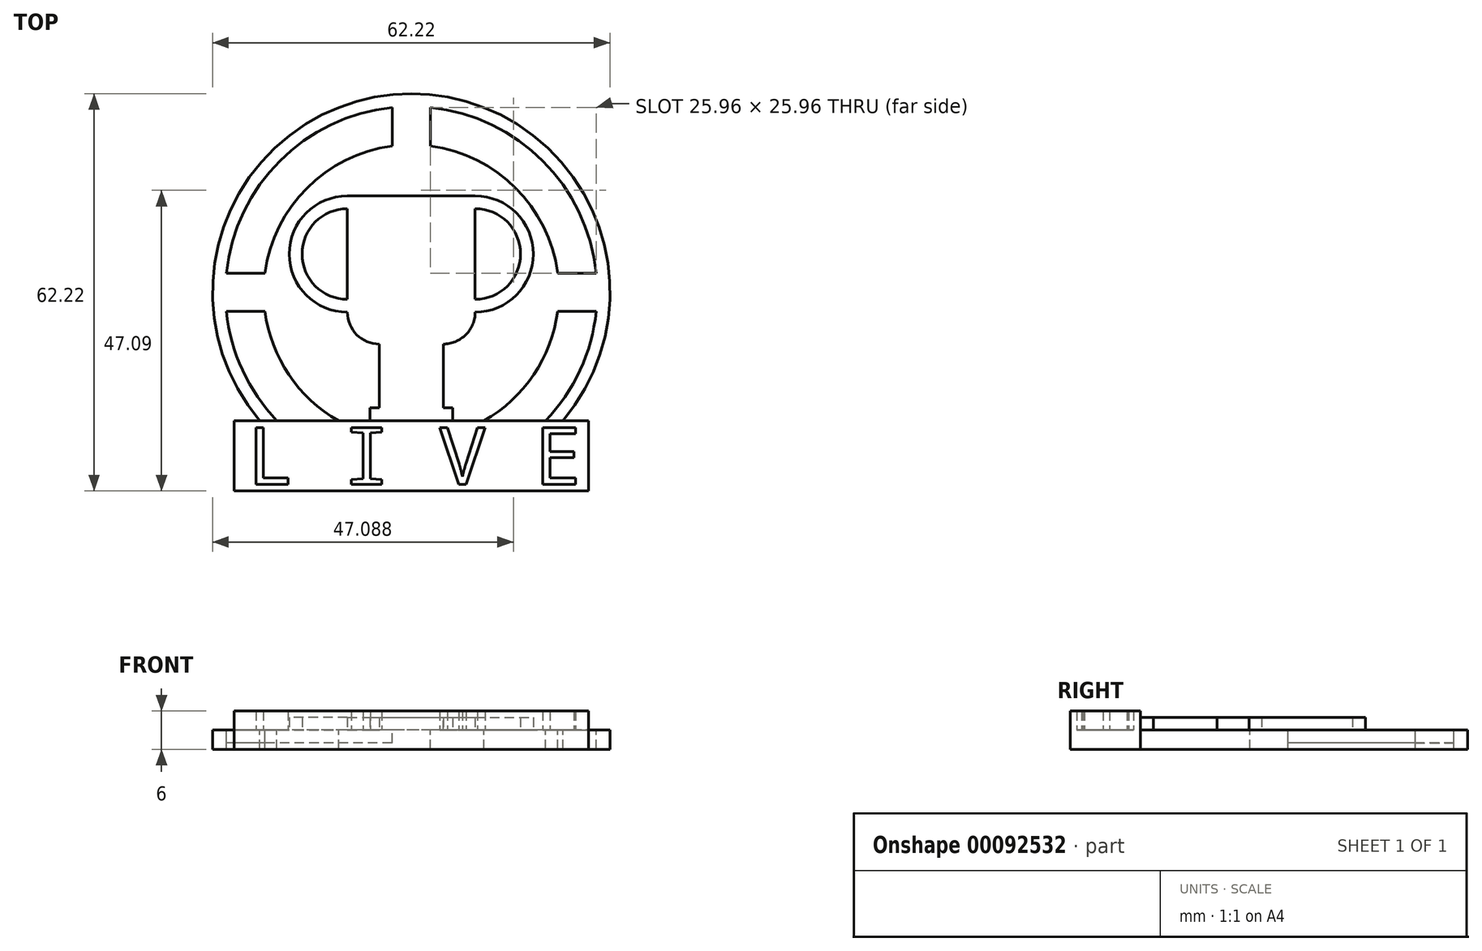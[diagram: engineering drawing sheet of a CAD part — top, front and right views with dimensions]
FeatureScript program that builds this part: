
annotation { "Feature Type Name" : "Feature", "Feature Type Description" : "" }
export const myFeature = defineFeature(function(context is Context, id is Id, definition is map)
    precondition{}
    {
        {
            var Q0;
            Q0=qCreatedBy(makeId("Top.planeOp"),FACE);
            var sketch = newSketch(context, id + "F0", { "sketchPlane" : qUnion([Q0])});
            skText(sketch, "E0", { "text": "L I V E", "fontName": "DroidSansMono.ttf"});
            skPoint(sketch, "E1", {"position": v(-23.74, 9) * mm});
            skPoint(sketch, "E2", {"position": v(23.74, 9) * mm});
            skPoint(sketch, "E3.third.point", {"position": v(14.12, 78.19) * mm});
            const initialGuessF0  = {"E0": [-0.02574, 0, 1, 0, 0.009]};
            skSetInitialGuess(sketch, initialGuessF0);
            skSolve(sketch);
        }
        {
            var Q0;
            Q0=qCreatedBy(makeId("Top.planeOp"),FACE);
            var sketch = newSketch(context, id + "F1", { "sketchPlane" : qUnion([Q0])});
            skLineSegment(sketch, "E4", {"start": v(-27.74, -1) * mm, "end": v(27.74, -1) * mm});
            skLineSegment(sketch, "E5", {"start": v(27.74, -1) * mm, "end": v(27.74, 10) * mm});
            skLineSegment(sketch, "E6", {"start": v(27.74, 10) * mm, "end": v(-27.74, 10) * mm});
            skLineSegment(sketch, "E7", {"start": v(-27.74, 10) * mm, "end": v(-27.74, -1) * mm});
            skSolve(sketch);
        }
        {
            var Q0;
            Q0 = qSketchRegion(id + "F1", true);
            extrude(context, id + "F2", {"entities" : qUnion([Q0]), "oppositeDirection" : true, "depth" : 3 * mm});
        }
        {
            var Q0;
            Q0=qCreatedBy(makeId("Top.planeOp"),FACE);
            var sketch = newSketch(context, id + "F3", { "sketchPlane" : qUnion([Q0])});
            skPoint(sketch, "E8", {"position": v(-23.74, 10) * mm});
            skPoint(sketch, "E9", {"position": v(23.74, 10) * mm});
            skArc(sketch, "E10", {"start": v(23.74, 10) * mm, "mid": v(0, 61.22) * mm, "end": v(-23.74, 10) * mm});
            skPoint(sketch, "E10.third.point", {"position": v(0, 61.22) * mm});
            skLineSegment(sketch, "E11", {"start": v(0, 30.11) * mm, "end": v(0, 61.22) * mm, "construction": true});
            skArc(sketch, "E12", {"start": v(21.05, 10) * mm, "mid": v(26.43, 17.9) * mm, "end": v(28.96, 27.11) * mm});
            skLineSegment(sketch, "E13", {"start": v(-31.11, 30.11) * mm, "end": v(0, 30.11) * mm, "construction": true});
            skArc(sketch, "E14", {"start": v(11.39, 10) * mm, "mid": v(19.17, 17.2) * mm, "end": v(22.92, 27.11) * mm});
            skLineSegment(sketch, "E15", {"start": v(-23.74, 10) * mm, "end": v(23.74, 10) * mm});
            skLineSegment(sketch, "E16.trimOffspring", {"start": v(-3, 53.03) * mm, "end": v(-3, 59.07) * mm});
            skLineSegment(sketch, "E17.trimOffspring", {"start": v(3, 53.03) * mm, "end": v(3, 59.07) * mm});
            skLineSegment(sketch, "E18.trimOffspring", {"start": v(-22.92, 33.11) * mm, "end": v(-28.96, 33.11) * mm});
            skLineSegment(sketch, "E19.trimOffspring", {"start": v(-22.92, 27.11) * mm, "end": v(-28.96, 27.11) * mm});
            skArc(sketch, "E20.trimOffspring", {"start": v(-22.92, 27.11) * mm, "mid": v(-19.17, 17.2) * mm, "end": v(-11.39, 10) * mm});
            skArc(sketch, "E21.trimOffspring", {"start": v(-28.96, 27.11) * mm, "mid": v(-26.43, 17.9) * mm, "end": v(-21.05, 10) * mm});
            skArc(sketch, "E22.trimOffspring", {"start": v(-3, 53.03) * mm, "mid": v(-16.34, 46.45) * mm, "end": v(-22.92, 33.11) * mm});
            skArc(sketch, "E23.trimOffspring", {"start": v(-3, 59.07) * mm, "mid": v(-20.59, 50.7) * mm, "end": v(-28.96, 33.11) * mm});
            skLineSegment(sketch, "E24.trimOffspring", {"start": v(22.92, 33.11) * mm, "end": v(28.96, 33.11) * mm});
            skLineSegment(sketch, "E25.trimOffspring", {"start": v(22.92, 27.11) * mm, "end": v(28.96, 27.11) * mm});
            skArc(sketch, "E26.trimOffspring", {"start": v(22.92, 33.11) * mm, "mid": v(16.34, 46.45) * mm, "end": v(3, 53.03) * mm});
            skArc(sketch, "E27.trimOffspring", {"start": v(28.96, 33.11) * mm, "mid": v(20.59, 50.7) * mm, "end": v(3, 59.07) * mm});
            skSolve(sketch);
        }
        {
            var Q0;
            {var subQ1=sQuery(id+"F3.wireOp",EDGE,"E10");Q0=makeQuery(id+"F3.imprint","IMPRINT",FACE,{"disambiguationData":[TD([[makeQuery(id+"F3.imprint","IMPRINT",EDGE,{"derivedFrom":subQ1}),1.0]])]});}
            var Q1;
            Q1=makeQuery(id+"F2.opExtrude","CAP_FACE",FACE,{"disambiguationData":[OSD([sQuery(id+"F1.wireOp",EDGE,"E4"),sQuery(id+"F1.wireOp",EDGE,"E5"),sQuery(id+"F1.wireOp",EDGE,"E6"),sQuery(id+"F1.wireOp",EDGE,"E7")])],"isStart":false});
            extrude(context, id + "F4", {"entities" : qUnion([Q0]), "operationType" : NewBodyOperationType.ADD, "oppositeDirection" : true, "endBoundEntityFace" : qUnion([Q1]), "depth" : 3 * mm});
        }
        {
            var Q0;
            Q0=makeQuery(id+"F4.boolean.opBoolean","MERGE",FACE,{"derivedFrom":[makeQuery(id+"F2.opExtrude","CAP_FACE",FACE,{"disambiguationData":[OSD([sQuery(id+"F1.wireOp",EDGE,"E4"),sQuery(id+"F1.wireOp",EDGE,"E5"),sQuery(id+"F1.wireOp",EDGE,"E6"),sQuery(id+"F1.wireOp",EDGE,"E7")])],"isStart":true}),makeQuery(id+"F4.opExtrude","CAP_FACE",FACE,{"disambiguationData":[OSD([sQuery(id+"F3.wireOp",EDGE,"E10"),sQuery(id+"F3.wireOp",EDGE,"E12"),sQuery(id+"F3.wireOp",EDGE,"E14"),sQuery(id+"F3.wireOp",EDGE,"E15"),sQuery(id+"F3.wireOp",EDGE,"E16.trimOffspring"),sQuery(id+"F3.wireOp",EDGE,"E17.trimOffspring"),sQuery(id+"F3.wireOp",EDGE,"E18.trimOffspring"),sQuery(id+"F3.wireOp",EDGE,"E19.trimOffspring"),sQuery(id+"F3.wireOp",EDGE,"E20.trimOffspring"),sQuery(id+"F3.wireOp",EDGE,"E21.trimOffspring"),sQuery(id+"F3.wireOp",EDGE,"E22.trimOffspring"),sQuery(id+"F3.wireOp",EDGE,"E23.trimOffspring"),sQuery(id+"F3.wireOp",EDGE,"E24.trimOffspring"),sQuery(id+"F3.wireOp",EDGE,"E25.trimOffspring"),sQuery(id+"F3.wireOp",EDGE,"E26.trimOffspring"),sQuery(id+"F3.wireOp",EDGE,"E27.trimOffspring")])],"isStart":true})]});
            var sketch = newSketch(context, id + "F5", { "sketchPlane" : qUnion([Q0])});
            skLineSegment(sketch, "E28.bottom", {"start": v(-6.5, 12) * mm, "end": v(-5, 12) * mm});
            skLineSegment(sketch, "E28.top", {"start": v(-6.5, 10) * mm, "end": v(6.5, 10) * mm});
            skLineSegment(sketch, "E28.left", {"start": v(-6.5, 12) * mm, "end": v(-6.5, 10) * mm});
            skLineSegment(sketch, "E28.right", {"start": v(6.5, 12) * mm, "end": v(6.5, 10) * mm});
            skLineSegment(sketch, "E29", {"start": v(11.39, 10) * mm, "end": v(11.39, 15) * mm, "construction": true});
            skLineSegment(sketch, "E30", {"start": v(-11.39, 10) * mm, "end": v(-11.39, 15) * mm, "construction": true});
            skLineSegment(sketch, "E31", {"start": v(-5, 12) * mm, "end": v(-5, 22) * mm});
            skLineSegment(sketch, "E32", {"start": v(5, 12) * mm, "end": v(5, 22) * mm});
            skLineSegment(sketch, "E33", {"start": v(5, 22) * mm, "end": v(5, 22) * mm});
            skLineSegment(sketch, "E34.trimOffspring", {"start": v(5, 12) * mm, "end": v(6.5, 12) * mm});
            skLineSegment(sketch, "E35", {"start": v(-5, 22) * mm, "end": v(-5, 22) * mm});
            skLineSegment(sketch, "E36", {"start": v(-10, 29) * mm, "end": v(-10, 43.21) * mm});
            skLineSegment(sketch, "E37", {"start": v(-10, 45.21) * mm, "end": v(10, 45.21) * mm});
            skLineSegment(sketch, "E38", {"start": v(10, 43.21) * mm, "end": v(10, 29) * mm});
            skPoint(sketch, "E39.visualSharp", {"position": v(10, 22) * mm});
            skArc(sketch, "E39.filletArc", {"start": v(5, 22) * mm, "mid": v(8.54, 23.46) * mm, "end": v(10, 27) * mm});
            skPoint(sketch, "E40.visualSharp", {"position": v(-10, 22) * mm});
            skArc(sketch, "E40.filletArc", {"start": v(-10, 27) * mm, "mid": v(-8.54, 23.46) * mm, "end": v(-5, 22) * mm});
            skArc(sketch, "E41", {"start": v(10, 27) * mm, "mid": v(19.1, 36.1) * mm, "end": v(10, 45.21) * mm});
            skArc(sketch, "E42", {"start": v(-10, 45.21) * mm, "mid": v(-19.1, 36.1) * mm, "end": v(-10, 27) * mm});
            skArc(sketch, "E43", {"start": v(-10, 43.21) * mm, "mid": v(-17.1, 36.1) * mm, "end": v(-10, 29) * mm});
            skArc(sketch, "E44", {"start": v(10, 29) * mm, "mid": v(17.1, 36.1) * mm, "end": v(10, 43.21) * mm});
            skSolve(sketch);
        }
        {
            var Q0;
            Q0 = qSketchRegion(id + "F5", true);
            extrude(context, id + "F6", {"entities" : qUnion([Q0]), "operationType" : NewBodyOperationType.ADD, "depth" : 2 * mm, "hasSecondDirection" : true, "secondDirectionOppositeDirection" : true, "secondDirectionDepth" : 2 * mm});
        }
        {
            var Q0;
            Q0=makeQuery(id+"F5.imprint","IMPRINT",FACE,{"disambiguationData":[TD([[makeQuery(id+"F5.imprint","IMPRINT",EDGE,{"derivedFrom":sQuery(id+"F5.wireOp",EDGE,"E28.bottom")}),1.0]])]});
            var sketch = newSketch(context, id + "F7", { "sketchPlane" : qUnion([Q0])});
            skLineSegment(sketch, "E45.bottom", {"start": v(27.74, -1) * mm, "end": v(-27.74, -1) * mm});
            skLineSegment(sketch, "E45.top", {"start": v(27.74, 10) * mm, "end": v(-27.74, 10) * mm});
            skLineSegment(sketch, "E45.left", {"start": v(27.74, -1) * mm, "end": v(27.74, 10) * mm});
            skLineSegment(sketch, "E45.right", {"start": v(-27.74, -1) * mm, "end": v(-27.74, 10) * mm});
            skSolve(sketch);
        }
        {
            var Q0;
            Q0 = qSketchRegion(id + "F7", true);
            extrude(context, id + "F8", {"entities" : qUnion([Q0]), "operationType" : NewBodyOperationType.ADD, "depth" : 3 * mm});
        }
        {
            var Q0;
            Q0 = qSketchRegion(id + "F0", true);
            extrude(context, id + "F9", {"entities" : qUnion([Q0]), "operationType" : NewBodyOperationType.REMOVE, "endBound" : BoundingType.THROUGH_ALL, "depth" : 3 * mm});
        }
        {
            var Q0;
            Q0=makeQuery(id+"F4.boolean.opBoolean","MERGE",FACE,{"derivedFrom":[makeQuery(id+"F2.opExtrude","CAP_FACE",FACE,{"disambiguationData":[OSD([sQuery(id+"F1.wireOp",EDGE,"E4"),sQuery(id+"F1.wireOp",EDGE,"E5"),sQuery(id+"F1.wireOp",EDGE,"E6"),sQuery(id+"F1.wireOp",EDGE,"E7")])],"isStart":false}),makeQuery(id+"F4.opExtrude","CAP_FACE",FACE,{"disambiguationData":[OSD([sQuery(id+"F3.wireOp",EDGE,"E10"),sQuery(id+"F3.wireOp",EDGE,"E12"),sQuery(id+"F3.wireOp",EDGE,"E14"),sQuery(id+"F3.wireOp",EDGE,"E15"),sQuery(id+"F3.wireOp",EDGE,"E16.trimOffspring"),sQuery(id+"F3.wireOp",EDGE,"E17.trimOffspring"),sQuery(id+"F3.wireOp",EDGE,"E18.trimOffspring"),sQuery(id+"F3.wireOp",EDGE,"E19.trimOffspring"),sQuery(id+"F3.wireOp",EDGE,"E20.trimOffspring"),sQuery(id+"F3.wireOp",EDGE,"E21.trimOffspring"),sQuery(id+"F3.wireOp",EDGE,"E22.trimOffspring"),sQuery(id+"F3.wireOp",EDGE,"E23.trimOffspring"),sQuery(id+"F3.wireOp",EDGE,"E24.trimOffspring"),sQuery(id+"F3.wireOp",EDGE,"E25.trimOffspring"),sQuery(id+"F3.wireOp",EDGE,"E26.trimOffspring"),sQuery(id+"F3.wireOp",EDGE,"E27.trimOffspring")])],"isStart":false})]});
            var sketch = newSketch(context, id + "F10", { "sketchPlane" : qUnion([Q0])});
            skArc(sketch, "E46", {"start": v(-28.96, -33.11) * mm, "mid": v(-20.59, -50.7) * mm, "end": v(-3, -59.07) * mm});
            skArc(sketch, "E47", {"start": v(-22.92, -33.11) * mm, "mid": v(-16.34, -46.45) * mm, "end": v(-3, -53.03) * mm});
            skLineSegment(sketch, "E48", {"start": v(-3, -59.07) * mm, "end": v(-3, -53.03) * mm});
            skLineSegment(sketch, "E49", {"start": v(-22.92, -33.11) * mm, "end": v(-28.96, -33.11) * mm});
            skSolve(sketch);
        }
        {
            var Q0;
            Q0 = qSketchRegion(id + "F10", true);
            extrude(context, id + "F11", {"entities" : qUnion([Q0]), "operationType" : NewBodyOperationType.ADD, "oppositeDirection" : true, "depth" : 1 * mm});
        }
    });
